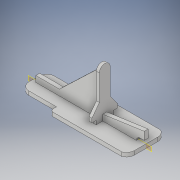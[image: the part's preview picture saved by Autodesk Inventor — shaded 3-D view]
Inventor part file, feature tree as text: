
AUTODESK INVENTOR PART (.ipt)
format: ipt  version: 2017 (Build 210142000, 142)  size: 225,280 bytes
history: native  units: in
note: dims shown in document units (in); Inventor stores cm internally (conversion verified against a paired STEP export)
features: sketch x8, extrude x7, plane x1, fillet x1
ambient origin geometry x8: Origin, YZ Plane, XZ Plane, XY Plane, X Axis, Y Axis, Z Axis, Center Point
bodies: Solid1 (feature_tree)
feature tree (17):
  extrude  "Extrusion1"  TaperAngle=90.0deg  [1 undecoded]
  sketch  "Sketch2"  dims[d9=0.1575in d10=90.0deg]
  plane  "Work Plane1"
  extrude  "Extrusion2"  TaperAngle=90.0deg  [1 undecoded]
  extrude  "Extrusion3"  Depth=0.0787in TaperAngle=0.0deg
  extrude  "Extrusion4"  TaperAngle=90.0deg  [1 undecoded]
  fillet  "Fillet1"  Radius=0.1575in
  extrude  "Extrusion5"  Depth=0.5118in
  extrude  "Extrusion6"  Depth=0.2165in
  extrude  "Extrusion7"  TaperAngle=90.0deg  [1 undecoded]
  sketch  "Sketch1"  dims[d7=0.1575in d8=90.0deg]
  sketch  "Sketch3"  dims[d11=0.1575in d12=0.0787in d13=0.0in]
  sketch  "Sketch4"  dims[d15=90.0deg d17=90.0deg d18=0.1575in]
  sketch  "Sketch5"  dims[d22=0.0787in d23=0.0in d26=0.5118in]
  sketch  "Sketch6"  dims[d27=0.1575in d28=0.2165in]
  sketch  "Sketch7"  dims[d29=0.5118in d30=90.0deg]
  sketch  "Sketch8"  dims[d31=0.0591in d32=0.0in d34=0.2362in d35=0.2756in d36=0.1575in d37=0.0in d38=0.1181in d39=0.0394in d40=0.0394in d41=0.7874in d42=0.0in d43=0.3543in d44=0.0394in d45=0.0in d46=0.0098in d47=90.0deg d48=0.0098in d49=90.0deg d50=0.3937in d51=0.0in]
note: 4 required parameter values undecoded (feature->parameter linkage not recoverable at this tier; creation-order binding heuristic only, values carry confidence <= 0.55)
